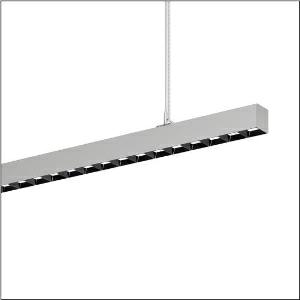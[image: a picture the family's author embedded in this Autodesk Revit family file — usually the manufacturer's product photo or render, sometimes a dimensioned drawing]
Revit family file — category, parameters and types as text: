
# Revit family: silica_r__21_51mx32tctds_853f
name_source: partatom
category: Lighting Fixtures
units: mm (PartAtom-declared; Revit-internal decimal feet)

## family parameters
Cut with Voids When Loaded = No
Host = Face
Light Source = No
Part Type = Normal
Room Calculation Point = No
Round Connector Dimension = Use Diameter
Shared = No

## types (1)
- --- (1 x LED, 15540 lm, 133.6 W, 6500K)
    Apparent Load = 134 VA
    CIE Flux Codes = 84 99 100 60 100
    Color Rendering = 80
    Color Temperature = 6500K
    Default Elevation = 1800 mm
    Description = Silica® 21, office luminaire, primary light control with darklight reflector, of PMMA, black, CAT 2 (L<= 3000cd/m²), light emission: direct/indirect distribution, primary light characteristic: symmetric, installation type: suspended mounting, LED, rated luminous flux: 15.540lm, luminous efficacy: 111lm/W, light colour: 8tw, colour temperature: 2700..6500K, control gear: ECG DALI, with terminal, 3+2-pole, max. 2.5mm², mains connection: 220..240V, AC, 50/60Hz, rated input power: 140.3W, luminaire housing, of aluminium, metallic grey (RAL 9006), length: 3.004mm, width: 53mm, height: 53mm, protection rating (complete): IP20, insulation class (complete): insulation class I (protective earthing), certification: CE, permissible operating ambient temperature: 0..+35°C, standard: EN 50419, packaging unit: 1 piece
    Height = 53 mm
    Lamp = 1 x LED
    Lamp Light Flux = 15540 lm
    Lamp Power = 133.6 W
    Lamp count = 1
    Length = 3004 mm
    Luminous efficacy = 116 lm/W
    Manufacturer = Siteco
    ModVariant = No
    Model = 51MX32TCTDS
    Mounting Place = Ceiling
    Mounting Type = Pendant
    Number of Poles = 1
    OnlyDefault = Yes
    Power Factor = 1
    Product Name = Silica® 21
    Product group = office luminaire | ceiling pendant
    ProductGroupID = 902
    Protection Class = Protection class I
    Protection Degree = IP 20
    RLX_Detail_Level = 1
    RLX_Emergency_Light_Flux = 0 lm
    RLX_Emergency_Type = 0
    RLX_Emergency_Type_DB = No
    RlxData = <blob elided: 62025 chars, md5=9a8f402c>
    Socket = socket
    Standby Power = 0 W
    System Light Flux = 15540 lm
    System Power = 134 W
    Type Comments = individual setting
    Type Image = l_1335859.jpg
    URL = http://relux.com
    VarID = @adj_109717
    Voltage = 0 V
    Weight = 0.00 kg
    Width = 53 mm

## geometry (parser evidence)
native form markers: Blend x4, Sweep x12
no freeform markers — native parametric forms only
